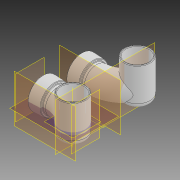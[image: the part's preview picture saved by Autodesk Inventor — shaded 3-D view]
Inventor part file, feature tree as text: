
AUTODESK INVENTOR PART (.ipt)
format: ipt  version: 2020 (Build 240168000, 168)  size: 471,552 bytes
history: native  units: mm
features: plane x7, sketch x5, other x3, extrude x2, fillet x2, sweep x1, shell x1, revolve x1, mirror x1, projected_geometry x1
ambient origin geometry x8: Origin, YZ Plane, XZ Plane, XY Plane, X Axis, Y Axis, Z Axis, Center Point
bodies: Solid1 (feature_tree), Solid2 (feature_tree)
feature tree (24):
  extrude  "Extrusion1"  Depth=37.5mm TaperAngle=0.0deg
  plane  "Work Plane2"
  extrude  "Extrusion2"  Depth=29.9mm
  sketch  "Sketch3"  dims[d5=42.5mm d6=12.2mm d7=-0.436332mm d8=24.5mm d12=-12.5mm]
  plane  "Work Plane3"
  other  "Work Point1"
  sweep  "Sweep2"
  fillet  "Fillet1"  Radius=24.5mm
  shell  "Shell1"  Thickness=-12.5mm
  plane  "Work Plane5"
  revolve  "Revolution1"  [1 undecoded]
  fillet  "Fillet2"  Radius=5.0mm
  plane  "Work Plane7"
  mirror  "Mirror3"
  sketch  "Sketch1"  dims[d0=25.5mm d1=37.5mm d2=0.0mm]
  plane  "Work Plane1"
  sketch  "Sketch2"  dims[d3=-55.0mm d4=29.9mm]
  projected_geometry  "Projected Loop1"
  sketch  "3D Sketch5"
  plane  "Work Plane4"
  other  "Work Axis1"
  sketch  "Sketch10"  dims[d14=15.0mm d15=0.0mm d16=0.0mm d17=5.0mm d18=1.5mm d21=90.0deg d22=2.0mm d23=90.0deg d24=0.5mm d25=-44.625mm]
  plane  "Work Plane6"
  other  "Pattern of Solid1:1"
note: 1 required parameter value undecoded (feature->parameter linkage not recoverable at this tier; creation-order binding heuristic only, values carry confidence <= 0.55)
